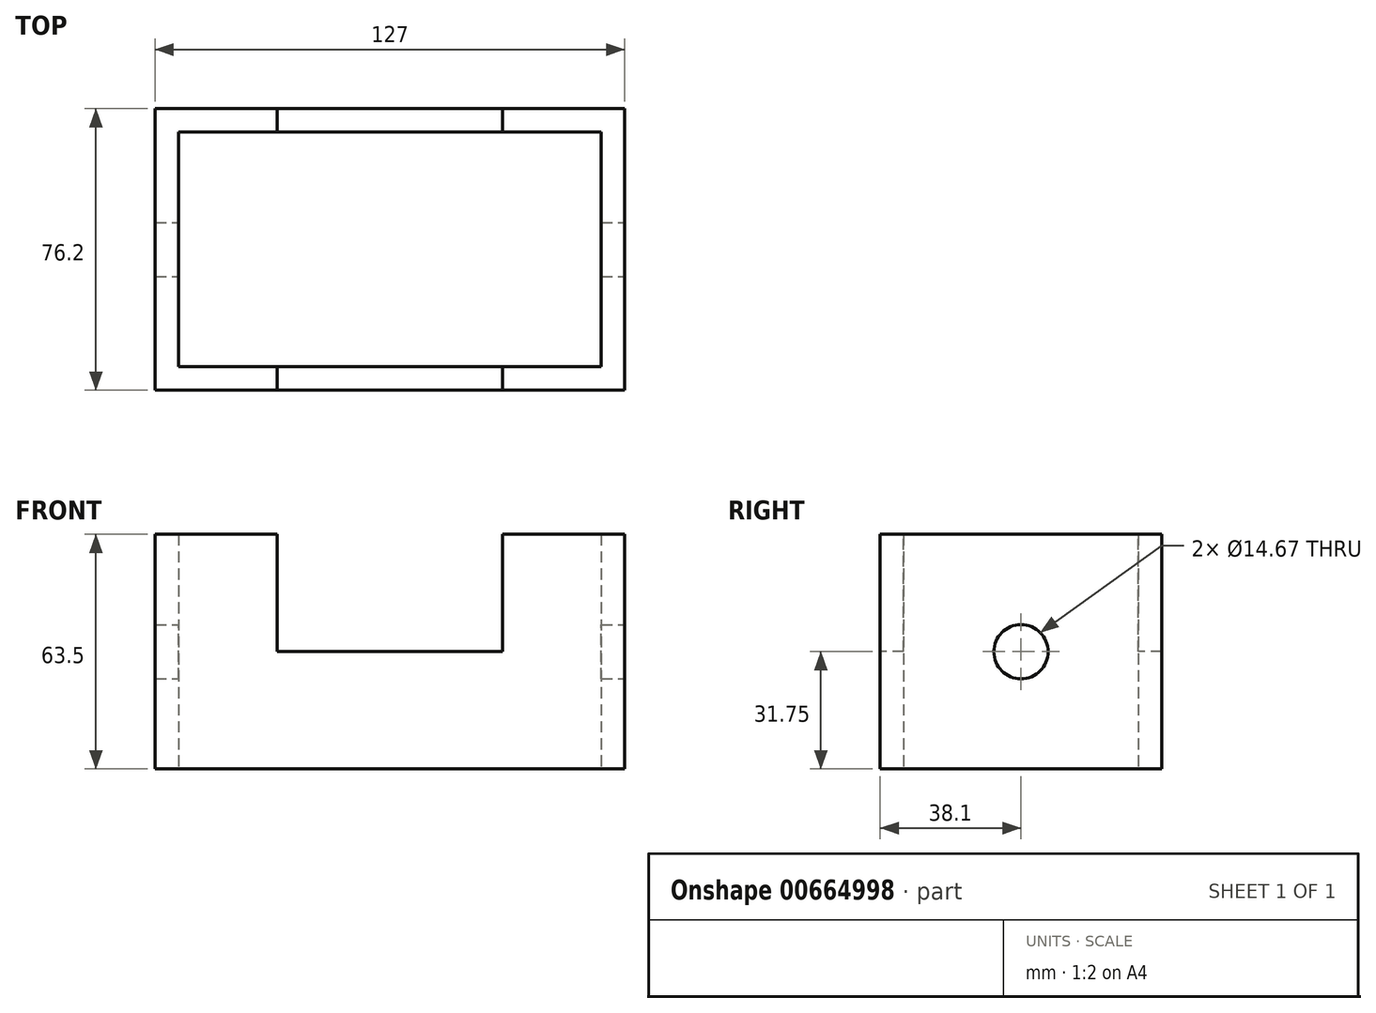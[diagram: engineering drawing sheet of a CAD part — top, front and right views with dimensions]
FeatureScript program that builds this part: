
annotation { "Feature Type Name" : "Feature", "Feature Type Description" : "" }
export const myFeature = defineFeature(function(context is Context, id is Id, definition is map)
    precondition{}
    {
        {
            var Q0;
            Q0=qCreatedBy(makeId("Top.planeOp"),FACE);
            var sketch = newSketch(context, id + "F0", { "sketchPlane" : qUnion([Q0])});
            skLineSegment(sketch, "E0.bottom", {"start": v(-63.5, 38.1) * mm, "end": v(63.5, 38.1) * mm});
            skLineSegment(sketch, "E0.top", {"start": v(-63.5, -38.1) * mm, "end": v(63.5, -38.1) * mm});
            skLineSegment(sketch, "E0.left", {"start": v(-63.5, 38.1) * mm, "end": v(-63.5, -38.1) * mm});
            skLineSegment(sketch, "E0.right", {"start": v(63.5, 38.1) * mm, "end": v(63.5, -38.1) * mm});
            skPoint(sketch, "E0.middle", {"position": v(0, 0) * mm});
            skLineSegment(sketch, "E1.bottom", {"start": v(-57.15, 31.75) * mm, "end": v(57.15, 31.75) * mm});
            skLineSegment(sketch, "E1.top", {"start": v(-57.15, -31.75) * mm, "end": v(57.15, -31.75) * mm});
            skLineSegment(sketch, "E1.left", {"start": v(-57.15, 31.75) * mm, "end": v(-57.15, -31.75) * mm});
            skLineSegment(sketch, "E1.right", {"start": v(57.15, 31.75) * mm, "end": v(57.15, -31.75) * mm});
            skSolve(sketch);
        }
        {
            var Q0;
            Q0=makeQuery(id+"F0.imprint","IMPRINT",FACE,{"disambiguationData":[TD([[makeQuery(id+"F0.imprint","IMPRINT",EDGE,{"derivedFrom":sQuery(id+"F0.wireOp",EDGE,"E0.bottom")}),-1.0]])]});
            extrude(context, id + "F1", {"entities" : qUnion([Q0]), "endBound" : BoundingType.SYMMETRIC, "depth" : 63.5 * mm, "offsetDistance" : 25.4 * mm});
        }
        {
            var Q0;
            Q0=makeQuery(id+"F1.opExtrude","SWEPT_FACE",FACE,{"disambiguationData":[OSD([sQuery(id+"F0.wireOp",EDGE,"E0.top")])]});
            var sketch = newSketch(context, id + "F2", { "sketchPlane" : qUnion([Q0])});
            skLineSegment(sketch, "E2", {"start": v(-30.48, 31.75) * mm, "end": v(-30.48, 0) * mm});
            skLineSegment(sketch, "E3", {"start": v(-30.48, 0) * mm, "end": v(0, 0) * mm});
            skLineSegment(sketch, "E4", {"start": v(0, 0) * mm, "end": v(30.48, 0) * mm});
            skLineSegment(sketch, "E5", {"start": v(30.48, 0) * mm, "end": v(30.48, 31.75) * mm});
            skLineSegment(sketch, "E6", {"start": v(30.48, 31.75) * mm, "end": v(-30.48, 31.75) * mm});
            skSolve(sketch);
        }
        {
            var Q0;
            Q0=makeQuery(id+"F2.imprint","IMPRINT",FACE,{"disambiguationData":[TD([[makeQuery(id+"F2.imprint","IMPRINT",EDGE,{"derivedFrom":sQuery(id+"F2.wireOp",EDGE,"E2")}),1.0]])]});
            extrude(context, id + "F3", {"entities" : qUnion([Q0]), "operationType" : NewBodyOperationType.REMOVE, "oppositeDirection" : true, "depth" : 101.6 * mm, "offsetDistance" : 25.4 * mm});
        }
        {
            var Q0;
            Q0=makeQuery(id+"F1.opExtrude","SWEPT_FACE",FACE,{"disambiguationData":[OSD([sQuery(id+"F0.wireOp",EDGE,"E0.right")])]});
            var sketch = newSketch(context, id + "F4", { "sketchPlane" : qUnion([Q0])});
            skCircle(sketch, "E7", {"center": v(0, 0) * mm, "radius": 7.34 * mm});
            skSolve(sketch);
        }
        {
            var Q0;
            Q0=makeQuery(id+"F4.imprint","IMPRINT",FACE,{"disambiguationData":[TD([[makeQuery(id+"F4.imprint","IMPRINT",EDGE,{"derivedFrom":sQuery(id+"F4.wireOp",EDGE,"E7")}),1.0]])]});
            extrude(context, id + "F5", {"entities" : qUnion([Q0]), "operationType" : NewBodyOperationType.REMOVE, "oppositeDirection" : true, "depth" : 127 * mm, "offsetDistance" : 25.4 * mm});
        }
    });
